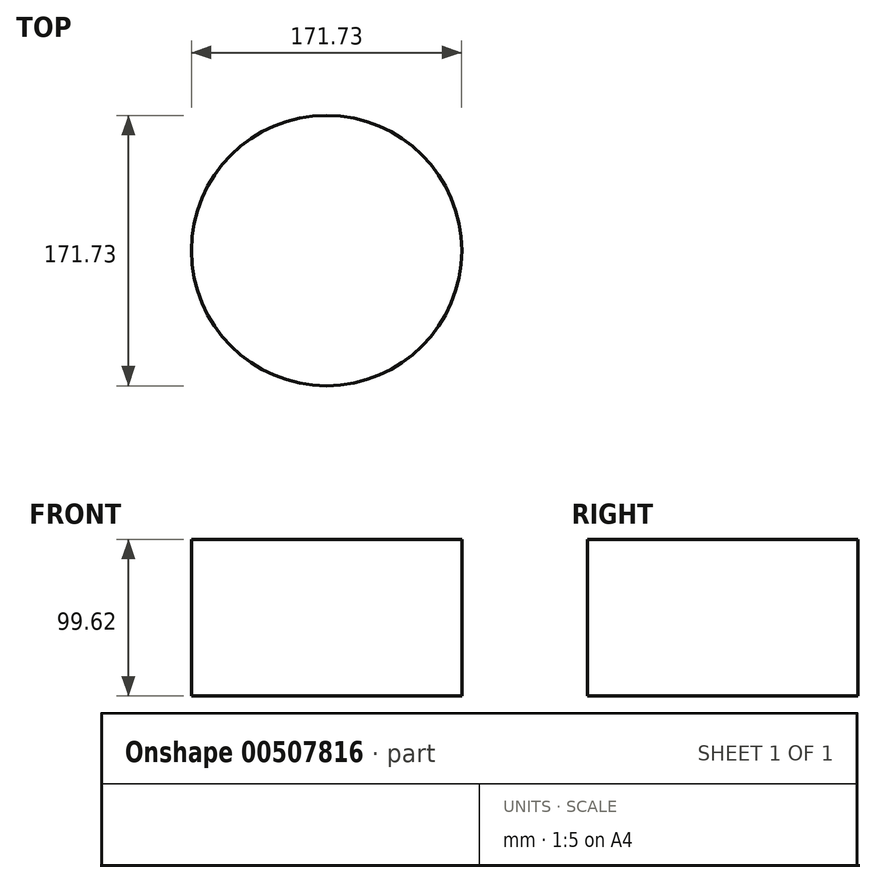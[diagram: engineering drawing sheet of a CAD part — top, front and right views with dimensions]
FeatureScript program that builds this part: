
annotation { "Feature Type Name" : "Feature", "Feature Type Description" : "" }
export const myFeature = defineFeature(function(context is Context, id is Id, definition is map)
    precondition{}
    {
        {
            var Q0;
            Q0=qCreatedBy(makeId("Top.planeOp"),FACE);
            var sketch = newSketch(context, id + "F0", { "sketchPlane" : qUnion([Q0])});
            skCircle(sketch, "E0", {"center": v(-18.25, 83.9) * mm, "radius": 85.87 * mm});
            skSolve(sketch);
        }
        {
            var Q0;
            Q0 = qSketchRegion(id + "F0", true);
            extrude(context, id + "F1", {"entities" : qUnion([Q0]), "depth" : 99.62 * mm});
        }
    });
